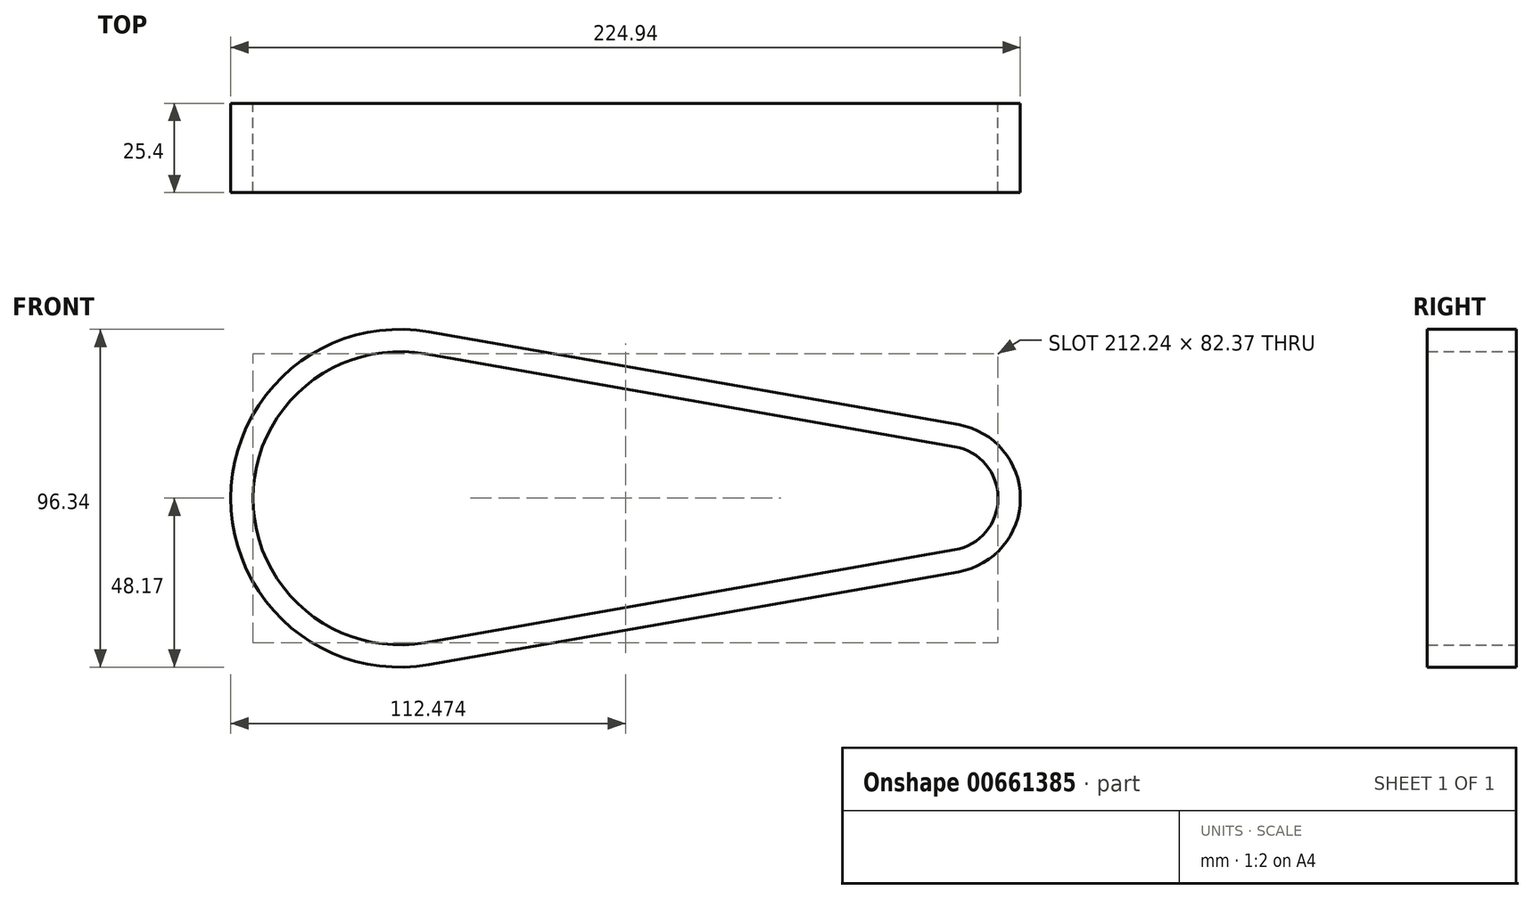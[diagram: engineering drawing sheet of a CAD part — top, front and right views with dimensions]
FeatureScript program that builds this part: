
annotation { "Feature Type Name" : "Feature", "Feature Type Description" : "" }
export const myFeature = defineFeature(function(context is Context, id is Id, definition is map)
    precondition{}
    {
        {
            var Q0;
            Q0=qCreatedBy(makeId("Front.planeOp"),FACE);
            var sketch = newSketch(context, id + "F0", { "sketchPlane" : qUnion([Q0])});
            skArc(sketch, "E0", {"start": v(-108.02, 41.19) * mm, "mid": v(-157.07, 0) * mm, "end": v(-108.02, -41.19) * mm});
            skArc(sketch, "E1", {"start": v(42.82, -14.71) * mm, "mid": v(55.17, 0) * mm, "end": v(42.82, 14.71) * mm});
            skLineSegment(sketch, "E2", {"start": v(-108.02, 41.19) * mm, "end": v(42.82, 14.71) * mm});
            skLineSegment(sketch, "E3", {"start": v(-108.02, -41.19) * mm, "end": v(42.82, -14.71) * mm});
            skLineSegment(sketch, "E4.0", {"start": v(-106.92, 47.44) * mm, "end": v(43.92, 20.97) * mm});
            skArc(sketch, "E4.1", {"start": v(-106.92, 47.44) * mm, "mid": v(-163.42, 0) * mm, "end": v(-106.92, -47.44) * mm});
            skLineSegment(sketch, "E4.2", {"start": v(-106.92, -47.44) * mm, "end": v(43.92, -20.97) * mm});
            skArc(sketch, "E4.3", {"start": v(43.92, -20.97) * mm, "mid": v(61.52, 0) * mm, "end": v(43.92, 20.97) * mm});
            skSolve(sketch);
        }
        {
            var Q0;
            Q0=makeQuery(id+"F0.imprint","IMPRINT",FACE,{"disambiguationData":[TD([[makeQuery(id+"F0.imprint","IMPRINT",EDGE,{"derivedFrom":sQuery(id+"F0.wireOp",EDGE,"E0")}),-1.0]])]});
            extrude(context, id + "F1", {"entities" : qUnion([Q0]), "depth" : 25.4 * mm, "offsetDistance" : 25.4 * mm});
        }
    });
